# Revit family: 706640001_Secador de Manos Forza
name_source: partatom
category: Plumbing Fixtures
units: mm (PartAtom-declared; Revit-internal decimal feet)

## family parameters
Always vertical = Yes
Cut with Voids When Loaded = No
Host = Wall
OmniClass Number = 23.40.20.21.14
OmniClass Title = Hand and Hair Dryers
Part Type = Normal
Room Calculation Point = No
Round Connector Dimension = Use Diameter
Shared = No

## types (1)
- Type 1
    Alto = 325 mm  [stored 1.06627 ft]
    Ancho = 278 mm
    Distancia de detección = 12 ± 3 cm
    Fabricante = Corona
    Frecuencia = 50 / 60 Hz
    Garantía = 5 años
    Material = Corona_Acero inoxidable
    Peso Bruto aprox = 6,0 kg. - 13,2 lbs
    Peso Neto aprox = 5,4 kg. - 11,9 lbs
    Potencia = 1800 W
    Potencia Motor = 550 W
    Profundidad = 172 mm  [stored 0.564304 ft]
    Referencia = 706640001
    URL = https://corona.co
    Velocidad del aire = 90 m /seg
    Voltaje = 110 - 120 V

note: [stored X ft] marks values corroborated as IEEE doubles in the binary element streams (Revit-internal decimal feet)

## geometry (parser evidence)
native form markers: Sweep x3
no freeform markers — native parametric forms only
